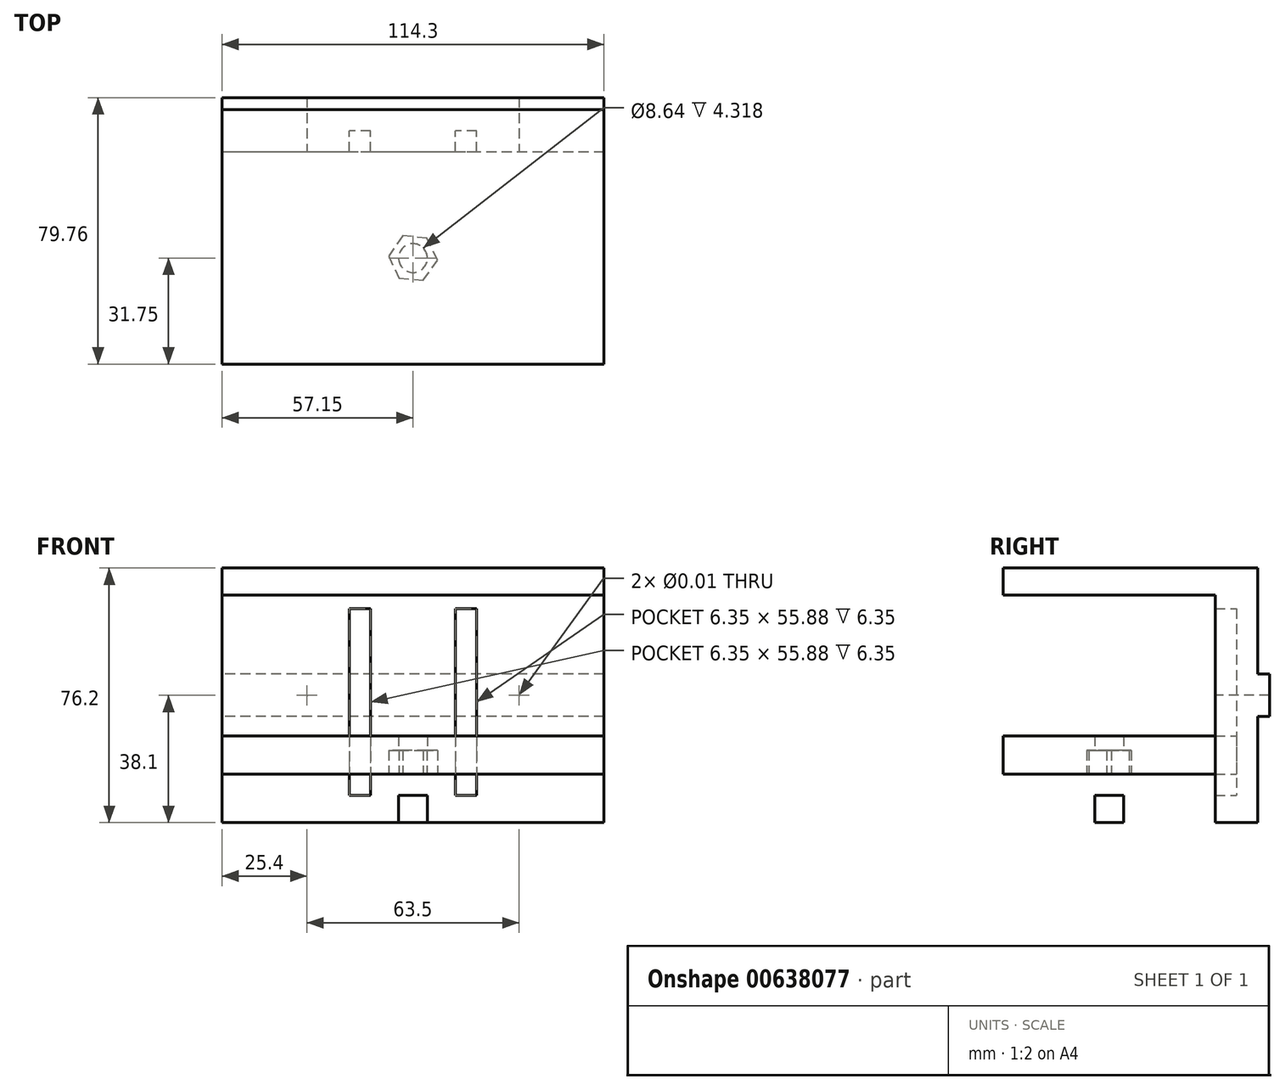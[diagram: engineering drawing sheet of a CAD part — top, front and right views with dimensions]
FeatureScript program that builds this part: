
annotation { "Feature Type Name" : "Feature", "Feature Type Description" : "" }
export const myFeature = defineFeature(function(context is Context, id is Id, definition is map)
    precondition{}
    {
        {
            var Q0;
            Q0=qCreatedBy(makeId("Right.planeOp"),FACE);
            var sketch = newSketch(context, id + "F0", { "sketchPlane" : qUnion([Q0])});
            skLineSegment(sketch, "E0", {"start": v(-38.1, -38.1) * mm, "end": v(38.1, -38.1) * mm});
            skLineSegment(sketch, "E1", {"start": v(38.1, 38.1) * mm, "end": v(-38.1, 38.1) * mm});
            skLineSegment(sketch, "E2", {"start": v(-38.1, 38.1) * mm, "end": v(-38.1, 29.97) * mm});
            skLineSegment(sketch, "E3", {"start": v(38.1, 38.1) * mm, "end": v(38.1, 6.35) * mm});
            skLineSegment(sketch, "E4", {"start": v(38.1, -6.35) * mm, "end": v(41.66, -6.35) * mm});
            skLineSegment(sketch, "E5", {"start": v(41.66, -6.35) * mm, "end": v(41.66, 6.35) * mm});
            skLineSegment(sketch, "E6", {"start": v(41.66, 6.35) * mm, "end": v(38.1, 6.35) * mm});
            skLineSegment(sketch, "E7.trimOffspring", {"start": v(38.1, -6.35) * mm, "end": v(38.1, -38.1) * mm});
            skLineSegment(sketch, "E8.1", {"start": v(25.4, 29.97) * mm, "end": v(-38.1, 29.97) * mm});
            skLineSegment(sketch, "E8.2", {"start": v(-38.1, -29.97) * mm, "end": v(25.4, -29.97) * mm});
            skLineSegment(sketch, "E8.3", {"start": v(25.4, 2.37) * mm, "end": v(25.4, -29.97) * mm});
            skLineSegment(sketch, "E8.4", {"start": v(25.4, 29.97) * mm, "end": v(25.4, 2.37) * mm});
            skLineSegment(sketch, "E9.trimOffspring", {"start": v(-38.1, -29.97) * mm, "end": v(-38.1, -38.1) * mm});
            skSolve(sketch);
        }
        {
            var Q0;
            Q0=makeQuery(id+"F0.imprint","IMPRINT",FACE,{"disambiguationData":[TD([[makeQuery(id+"F0.imprint","IMPRINT",EDGE,{"derivedFrom":sQuery(id+"F0.wireOp",EDGE,"E0")}),1.0]])]});
            extrude(context, id + "F1", {"entities" : qUnion([Q0]), "depth" : 114.3 * mm, "offsetDistance" : 25.4 * mm});
        }
        {
            var Q0;
            Q0=makeQuery(id+"F1.opExtrude","SWEPT_FACE",FACE,{"disambiguationData":[OSD([sQuery(id+"F0.wireOp",EDGE,"E8.3"),sQuery(id+"F0.wireOp",EDGE,"E8.4")])]});
            var sketch = newSketch(context, id + "F2", { "sketchPlane" : qUnion([Q0])});
            skLineSegment(sketch, "E10.0", {"start": v(25.4, 29.97) * mm, "end": v(25.4, -29.97) * mm});
            skLineSegment(sketch, "E11.0", {"start": v(88.9, 29.97) * mm, "end": v(88.9, -29.97) * mm});
            skLineSegment(sketch, "E12.0", {"start": v(114.3, 29.97) * mm, "end": v(0, 29.97) * mm});
            skCircle(sketch, "E13", {"center": v(25.4, 0) * mm, "radius": 4.32 * mm});
            skCircle(sketch, "E14", {"center": v(88.9, 0) * mm, "radius": 4.32 * mm});
            skSolve(sketch);
        }
        {
            var Q0;
            Q0=sQuery(id+"F2.wireOp",VERTEX,"E13.center");
            var Q1;
            Q1=sQuery(id+"F2.wireOp",VERTEX,"E14.center");
            var Q2;
            Q2=makeQuery(id+"F1.opExtrude","SWEPT_BODY",BODY,{"disambiguationData":[OSD([sQuery(id+"F0.wireOp",EDGE,"E0"),sQuery(id+"F0.wireOp",EDGE,"E1"),sQuery(id+"F0.wireOp",EDGE,"E2"),sQuery(id+"F0.wireOp",EDGE,"E3"),sQuery(id+"F0.wireOp",EDGE,"E4"),sQuery(id+"F0.wireOp",EDGE,"E5"),sQuery(id+"F0.wireOp",EDGE,"E6"),sQuery(id+"F0.wireOp",EDGE,"E7.trimOffspring"),sQuery(id+"F0.wireOp",EDGE,"E8.1"),sQuery(id+"F0.wireOp",EDGE,"E8.2"),sQuery(id+"F0.wireOp",EDGE,"E8.3"),sQuery(id+"F0.wireOp",EDGE,"E8.4"),sQuery(id+"F0.wireOp",EDGE,"E9.trimOffspring")])]});
            hole(context, id + "F3", {"style" : HoleStyle.SIMPLE, "endStyle" : HoleEndStyle.THROUGH, "standardTappedOrClearance" : lookupTablePath({ "standard" : "ANSI", "size" : "21/64 (0.33)", "type" : "Drilled" }), "standardBlindInLast" : lookupTablePath({ "standard" : "ANSI", "size" : "21/64", "type" : "Drilled" }), "holeDiameter" : 21 / 1625.6 * mm, "majorDiameter" : 6.35 * mm, "isTappedThrough" : true, "tappedDepth" : 12.7 * mm, "tapClearance" : 3, "locations" : qUnion([Q0, Q1]), "scope" : qUnion([Q2])});
        }
        {
            var Q0;
            Q0=makeQuery(id+"F1.opExtrude","SWEPT_FACE",FACE,{"disambiguationData":[OSD([sQuery(id+"F0.wireOp",EDGE,"E8.2")])]});
            var sketch = newSketch(context, id + "F4", { "sketchPlane" : qUnion([Q0])});
            skLineSegment(sketch, "E15.0", {"start": v(114.3, 25.4) * mm, "end": v(76.2, 25.4) * mm});
            skLineSegment(sketch, "E15.1", {"start": v(114.3, -38.1) * mm, "end": v(0, -38.1) * mm});
            skLineSegment(sketch, "E15.2", {"start": v(0, -38.1) * mm, "end": v(0, 25.4) * mm});
            skLineSegment(sketch, "E15.3", {"start": v(114.3, -38.1) * mm, "end": v(114.3, 25.4) * mm});
            skLineSegment(sketch, "E16.0", {"start": v(76.2, 31.75) * mm, "end": v(69.85, 31.75) * mm});
            skLineSegment(sketch, "E17.0", {"start": v(38.1, 25.4) * mm, "end": v(38.1, 31.75) * mm});
            skLineSegment(sketch, "E18.0", {"start": v(44.45, 25.4) * mm, "end": v(44.45, 31.75) * mm});
            skLineSegment(sketch, "E19.0", {"start": v(76.2, 25.4) * mm, "end": v(76.2, 31.75) * mm});
            skLineSegment(sketch, "E20.0", {"start": v(69.85, 25.4) * mm, "end": v(69.85, 31.75) * mm});
            skLineSegment(sketch, "E21.trimOffspring", {"start": v(38.1, 25.4) * mm, "end": v(0, 25.4) * mm});
            skLineSegment(sketch, "E22.trimOffspring", {"start": v(44.45, 31.75) * mm, "end": v(38.1, 31.75) * mm});
            skLineSegment(sketch, "E23.trimOffspring", {"start": v(69.85, 25.4) * mm, "end": v(44.45, 25.4) * mm});
            skLineSegment(sketch, "E24", {"start": v(57.15, -38.1) * mm, "end": v(57.15, 25.4) * mm});
            skCircle(sketch, "E25", {"center": v(57.15, -6.35) * mm, "radius": 4.32 * mm});
            skSolve(sketch);
        }
        {
            var Q0;
            {var subQ0=sQuery(id+"F4.wireOp",EDGE,"E25");var subQ1=sQuery(id+"F4.wireOp",EDGE,"E24");var subQ2=makeQuery(id+"F4.imprint","INTERSECT",VERTEX,{"disambiguationData":[OD(0.0)],"derivedFrom":[subQ1,subQ0]});Q0=makeQuery(id+"F4.imprint","IMPRINT",FACE,{"disambiguationData":[TD([[makeQuery(id+"F4.imprint","IMPRINT",EDGE,{"disambiguationData":[TD([[subQ2,-1.0]])],"derivedFrom":subQ1}),1.0]])]});}
            var Q1;
            {var subQ0=sQuery(id+"F4.wireOp",EDGE,"E25");var subQ1=sQuery(id+"F4.wireOp",EDGE,"E24");var subQ2=makeQuery(id+"F4.imprint","INTERSECT",VERTEX,{"disambiguationData":[OD(0.0)],"derivedFrom":[subQ1,subQ0]});Q1=makeQuery(id+"F4.imprint","IMPRINT",FACE,{"disambiguationData":[TD([[makeQuery(id+"F4.imprint","IMPRINT",EDGE,{"disambiguationData":[TD([[subQ2,-1.0]])],"derivedFrom":subQ1}),-1.0]])]});}
            extrude(context, id + "F5", {"entities" : qUnion([Q0, Q1]), "operationType" : NewBodyOperationType.REMOVE, "oppositeDirection" : true, "depth" : 12.7 * mm, "offsetDistance" : 25.4 * mm});
        }
        {
            var Q0;
            {var subQ0=sQuery(id+"F4.wireOp",EDGE,"E17.0");Q0=makeQuery(id+"F4.imprint","IMPRINT",FACE,{"disambiguationData":[TD([[makeQuery(id+"F4.imprint","IMPRINT",EDGE,{"derivedFrom":subQ0}),-1.0]])]});}
            var Q1;
            Q1=makeQuery(id+"F4.imprint","IMPRINT",FACE,{"disambiguationData":[TD([[makeQuery(id+"F4.imprint","IMPRINT",EDGE,{"derivedFrom":sQuery(id+"F4.wireOp",EDGE,"E16.0")}),1.0]])]});
            extrude(context, id + "F6", {"entities" : qUnion([Q0, Q1]), "operationType" : NewBodyOperationType.REMOVE, "depth" : 55.88 * mm, "offsetDistance" : 25.4 * mm});
        }
        {
            var Q0;
            {var subQ6=sQuery(id+"F4.wireOp",EDGE,"E15.2");Q0=makeQuery(id+"F4.imprint","IMPRINT",FACE,{"disambiguationData":[TD([[makeQuery(id+"F4.imprint","IMPRINT",EDGE,{"derivedFrom":subQ6}),-1.0]])]});}
            var Q1;
            {var subQ0=sQuery(id+"F4.wireOp",EDGE,"E17.0");Q1=makeQuery(id+"F4.imprint","IMPRINT",FACE,{"disambiguationData":[TD([[makeQuery(id+"F4.imprint","IMPRINT",EDGE,{"derivedFrom":subQ0}),-1.0]])]});}
            var Q2;
            Q2=makeQuery(id+"F4.imprint","IMPRINT",FACE,{"disambiguationData":[TD([[makeQuery(id+"F4.imprint","IMPRINT",EDGE,{"derivedFrom":sQuery(id+"F4.wireOp",EDGE,"E16.0")}),1.0]])]});
            var Q3;
            {var subQ8=sQuery(id+"F4.wireOp",EDGE,"E15.0");Q3=makeQuery(id+"F4.imprint","IMPRINT",FACE,{"disambiguationData":[TD([[makeQuery(id+"F4.imprint","IMPRINT",EDGE,{"derivedFrom":subQ8}),1.0]])]});}
            extrude(context, id + "F7", {"entities" : qUnion([Q0, Q1, Q2, Q3]), "depth" : 17.78 * mm, "offsetDistance" : 25.4 * mm, "hasSecondDirection" : true, "secondDirectionOppositeDirection" : false, "secondDirectionDepth" : 6.35 * mm});
        }
        {
            var Q0;
            Q0=makeQuery(id+"F7.opExtrude","CAP_FACE",FACE,{"disambiguationData":[OSD([sQuery(id+"F4.wireOp",EDGE,"E15.0"),sQuery(id+"F4.wireOp",EDGE,"E15.1"),sQuery(id+"F4.wireOp",EDGE,"E15.2"),sQuery(id+"F4.wireOp",EDGE,"E15.3"),sQuery(id+"F4.wireOp",EDGE,"E16.0"),sQuery(id+"F4.wireOp",EDGE,"E17.0"),sQuery(id+"F4.wireOp",EDGE,"E18.0"),sQuery(id+"F4.wireOp",EDGE,"E19.0"),sQuery(id+"F4.wireOp",EDGE,"E20.0"),sQuery(id+"F4.wireOp",EDGE,"E21.trimOffspring"),sQuery(id+"F4.wireOp",EDGE,"E22.trimOffspring"),sQuery(id+"F4.wireOp",EDGE,"E23.trimOffspring"),sQuery(id+"F4.wireOp",EDGE,"E25")])],"isStart":true});
            var sketch = newSketch(context, id + "F8", { "sketchPlane" : qUnion([Q0])});
            skCircle(sketch, "E26.cCircle", {"center": v(57.15, 6.35) * mm, "radius": 6.35 * mm, "construction": true});
            skLineSegment(sketch, "E26.0", {"start": v(52.92, 12.34) * mm, "end": v(60.22, 13) * mm});
            skLineSegment(sketch, "E26.1", {"start": v(60.22, 13) * mm, "end": v(64.45, 7.02) * mm});
            skLineSegment(sketch, "E26.2", {"start": v(64.45, 7.02) * mm, "end": v(61.38, 0.36) * mm});
            skLineSegment(sketch, "E26.3", {"start": v(61.38, 0.36) * mm, "end": v(54.08, -0.3) * mm});
            skLineSegment(sketch, "E26.4", {"start": v(54.08, -0.3) * mm, "end": v(49.85, 5.68) * mm});
            skLineSegment(sketch, "E26.5", {"start": v(49.85, 5.68) * mm, "end": v(52.92, 12.34) * mm});
            skPoint(sketch, "E26.0.midPoint", {"position": v(56.57, 12.67) * mm});
            skSolve(sketch);
        }
        {
            var Q0;
            Q0=makeQuery(id+"F8.imprint","IMPRINT",FACE,{"disambiguationData":[TD([[makeQuery(id+"F8.imprint","IMPRINT",EDGE,{"derivedFrom":sQuery(id+"F8.wireOp",EDGE,"E26.0")}),-1.0]])]});
            extrude(context, id + "F9", {"entities" : qUnion([Q0]), "operationType" : NewBodyOperationType.REMOVE, "oppositeDirection" : true, "depth" : 7.11 * mm, "offsetDistance" : 25.4 * mm});
        }
    });
